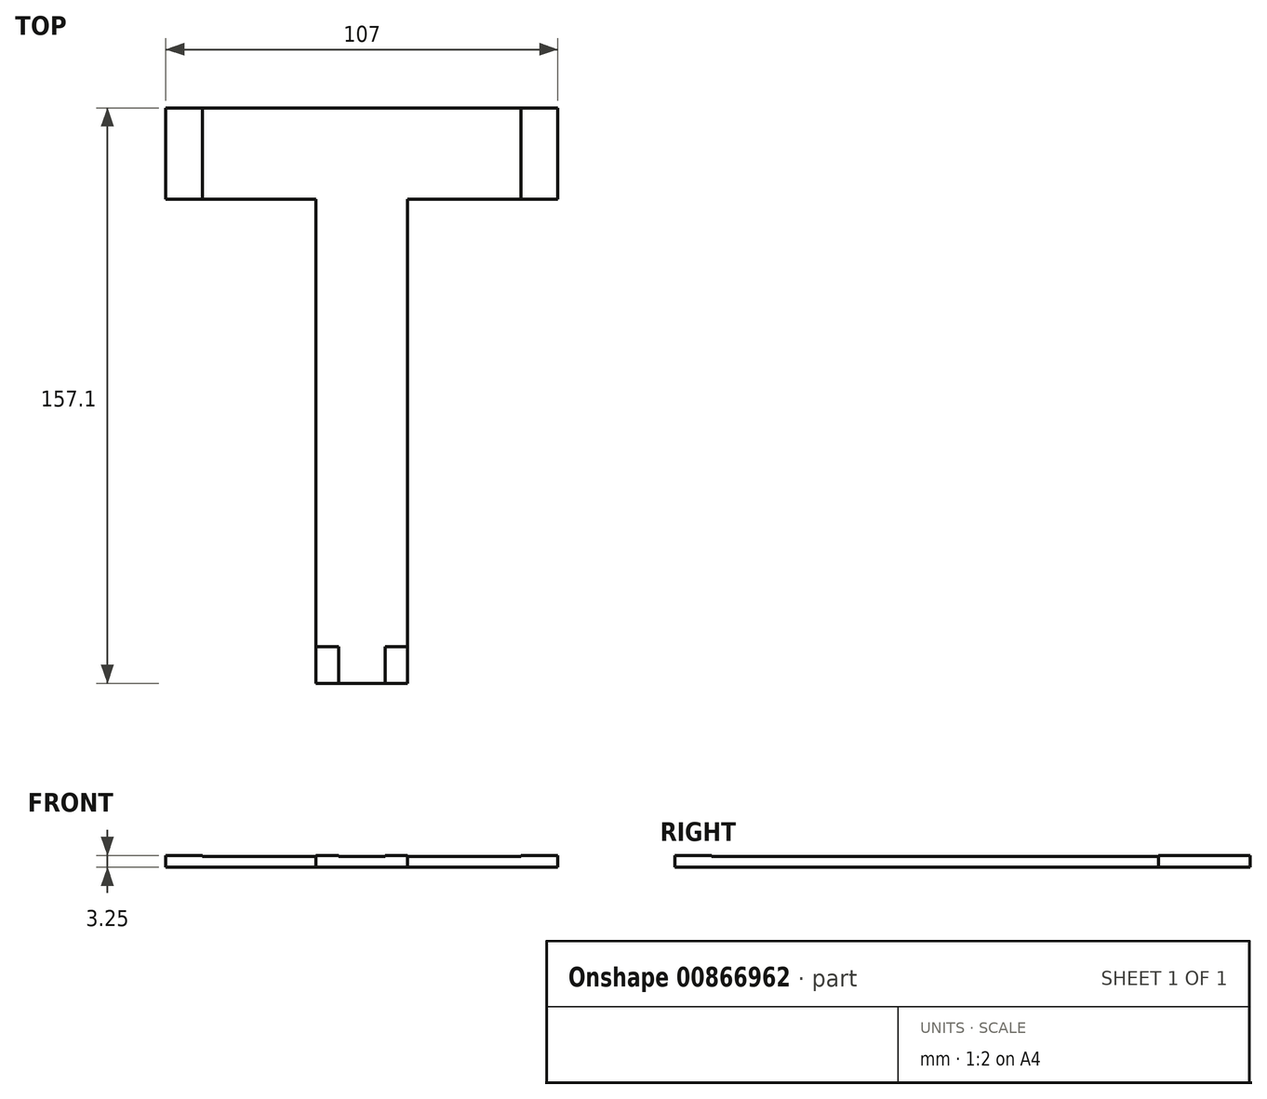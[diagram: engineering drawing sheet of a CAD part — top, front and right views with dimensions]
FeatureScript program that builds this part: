
annotation { "Feature Type Name" : "Feature", "Feature Type Description" : "" }
export const myFeature = defineFeature(function(context is Context, id is Id, definition is map)
    precondition{}
    {
        {
            var Q0;
            Q0=qCreatedBy(makeId("Top.planeOp"),FACE);
            var sketch = newSketch(context, id + "F0", { "sketchPlane" : qUnion([Q0])});
            skLineSegment(sketch, "E0.bottom", {"start": v(13.1, -94.8) * mm, "end": v(-11.9, -94.8) * mm});
            skLineSegment(sketch, "E0.top", {"start": v(13.1, 27.3) * mm, "end": v(-11.9, 27.3) * mm});
            skLineSegment(sketch, "E0.left", {"start": v(13.1, -94.8) * mm, "end": v(13.1, 27.3) * mm});
            skLineSegment(sketch, "E0.right", {"start": v(-11.9, -94.8) * mm, "end": v(-11.9, 27.3) * mm});
            skPoint(sketch, "E0.middle", {"position": v(0.6, -33.75) * mm});
            skLineSegment(sketch, "E1", {"start": v(0.6, 27.3) * mm, "end": v(0.6, 52.3) * mm});
            skLineSegment(sketch, "E2", {"start": v(0.6, 52.3) * mm, "end": v(-42.9, 52.3) * mm});
            skLineSegment(sketch, "E3", {"start": v(-42.9, 52.3) * mm, "end": v(-42.9, 27.3) * mm});
            skLineSegment(sketch, "E4", {"start": v(-42.9, 27.3) * mm, "end": v(-11.9, 27.3) * mm});
            skLineSegment(sketch, "E5", {"start": v(0.6, 52.3) * mm, "end": v(44.1, 52.3) * mm});
            skLineSegment(sketch, "E6", {"start": v(44.1, 52.3) * mm, "end": v(44.1, 27.3) * mm});
            skLineSegment(sketch, "E7", {"start": v(44.1, 27.3) * mm, "end": v(13.1, 27.3) * mm});
            skLineSegment(sketch, "E8", {"start": v(44.1, 52.3) * mm, "end": v(54.1, 52.3) * mm});
            skLineSegment(sketch, "E9", {"start": v(54.1, 52.3) * mm, "end": v(54.1, 27.3) * mm});
            skLineSegment(sketch, "E10", {"start": v(54.1, 27.3) * mm, "end": v(44.1, 27.3) * mm});
            skLineSegment(sketch, "E11", {"start": v(39.1, 52.3) * mm, "end": v(39.1, 27.3) * mm});
            skLineSegment(sketch, "E12", {"start": v(-36.9, 52.3) * mm, "end": v(-36.9, 27.3) * mm});
            skLineSegment(sketch, "E13", {"start": v(-42.9, 52.3) * mm, "end": v(-52.9, 52.3) * mm});
            skLineSegment(sketch, "E14", {"start": v(-52.9, 52.3) * mm, "end": v(-52.9, 27.3) * mm});
            skLineSegment(sketch, "E15", {"start": v(-52.9, 27.3) * mm, "end": v(-42.9, 27.3) * mm});
            skLineSegment(sketch, "E16", {"start": v(-18.95, -94.8) * mm, "end": v(-18.95, -89.8) * mm});
            skLineSegment(sketch, "E17", {"start": v(-11.9, -94.8) * mm, "end": v(-11.9, -104.8) * mm});
            skLineSegment(sketch, "E18", {"start": v(-11.9, -104.8) * mm, "end": v(13.1, -104.8) * mm});
            skLineSegment(sketch, "E19", {"start": v(13.1, -104.8) * mm, "end": v(13.1, -94.8) * mm});
            skLineSegment(sketch, "E20", {"start": v(-11.9, -89.8) * mm, "end": v(13.1, -89.8) * mm});
            skLineSegment(sketch, "E21", {"start": v(-5.76, -89.8) * mm, "end": v(-5.76, -104.8) * mm});
            skLineSegment(sketch, "E22", {"start": v(6.94, -89.8) * mm, "end": v(6.94, -104.8) * mm});
            skSolve(sketch);
        }
        {
            var Q0;
            {var subQ0=sQuery(id+"F0.wireOp",EDGE,"E3");Q0=makeQuery(id+"F0.imprint","IMPRINT",FACE,{"disambiguationData":[TD([[makeQuery(id+"F0.imprint","IMPRINT",EDGE,{"derivedFrom":subQ0}),1.0]])]});}
            var Q1;
            {var subQ1=sQuery(id+"F0.wireOp",EDGE,"E1");Q1=makeQuery(id+"F0.imprint","IMPRINT",FACE,{"disambiguationData":[TD([[makeQuery(id+"F0.imprint","IMPRINT",EDGE,{"derivedFrom":subQ1}),1.0]])]});}
            var Q2;
            {var subQ1=sQuery(id+"F0.wireOp",EDGE,"E1");Q2=makeQuery(id+"F0.imprint","IMPRINT",FACE,{"disambiguationData":[TD([[makeQuery(id+"F0.imprint","IMPRINT",EDGE,{"derivedFrom":subQ1}),-1.0]])]});}
            var Q3;
            {var subQ0=sQuery(id+"F0.wireOp",EDGE,"E6");Q3=makeQuery(id+"F0.imprint","IMPRINT",FACE,{"disambiguationData":[TD([[makeQuery(id+"F0.imprint","IMPRINT",EDGE,{"derivedFrom":subQ0}),-1.0]])]});}
            var Q4;
            {var subQ0=sQuery(id+"F0.wireOp",EDGE,"E22");var subQ1=sQuery(id+"F0.wireOp",EDGE,"E0.bottom");var subQ2=makeQuery(id+"F0.imprint","INTERSECT",VERTEX,{"derivedFrom":[subQ1,subQ0]});Q4=makeQuery(id+"F0.imprint","IMPRINT",FACE,{"disambiguationData":[TD([[makeQuery(id+"F0.imprint","IMPRINT",EDGE,{"disambiguationData":[TD([[subQ2,-1.0]])],"derivedFrom":subQ1}),1.0]])]});}
            var Q5;
            {var subQ0=sQuery(id+"F0.wireOp",EDGE,"E22");var subQ1=sQuery(id+"F0.wireOp",EDGE,"E0.bottom");var subQ2=makeQuery(id+"F0.imprint","INTERSECT",VERTEX,{"derivedFrom":[subQ1,subQ0]});Q5=makeQuery(id+"F0.imprint","IMPRINT",FACE,{"disambiguationData":[TD([[makeQuery(id+"F0.imprint","IMPRINT",EDGE,{"disambiguationData":[TD([[subQ2,-1.0]])],"derivedFrom":subQ1}),-1.0]])]});}
            var Q6;
            {var subQ0=sQuery(id+"F0.wireOp",EDGE,"E0.left");var subQ5=sQuery(id+"F0.wireOp",EDGE,"E20");var subQ6=makeQuery(id+"F0.imprint","INTERSECT",VERTEX,{"derivedFrom":[subQ0,subQ5]});Q6=makeQuery(id+"F0.imprint","IMPRINT",FACE,{"disambiguationData":[TD([[makeQuery(id+"F0.imprint","IMPRINT",EDGE,{"disambiguationData":[TD([[subQ6,1.0]])],"derivedFrom":subQ5}),-1.0]])]});}
            var Q7;
            {var subQ3=sQuery(id+"F0.wireOp",EDGE,"E20");var subQ5=sQuery(id+"F0.wireOp",EDGE,"E0.right");var subQ8=makeQuery(id+"F0.imprint","INTERSECT",VERTEX,{"derivedFrom":[subQ5,subQ3]});Q7=makeQuery(id+"F0.imprint","IMPRINT",FACE,{"disambiguationData":[TD([[makeQuery(id+"F0.imprint","IMPRINT",EDGE,{"disambiguationData":[TD([[subQ8,-1.0]])],"derivedFrom":subQ3}),1.0]])]});}
            var Q8;
            {var subQ0=sQuery(id+"F0.wireOp",EDGE,"E0.right");var subQ5=sQuery(id+"F0.wireOp",EDGE,"E20");var subQ6=makeQuery(id+"F0.imprint","INTERSECT",VERTEX,{"derivedFrom":[subQ0,subQ5]});Q8=makeQuery(id+"F0.imprint","IMPRINT",FACE,{"disambiguationData":[TD([[makeQuery(id+"F0.imprint","IMPRINT",EDGE,{"disambiguationData":[TD([[subQ6,-1.0]])],"derivedFrom":subQ5}),-1.0]])]});}
            extrude(context, id + "F1", {"entities" : qUnion([Q0, Q1, Q2, Q3, Q4, Q5, Q6, Q7, Q8]), "depth" : 3 * mm, "offsetDistance" : 25 * mm});
        }
        {
            var Q0;
            {var subQ0=sQuery(id+"F0.wireOp",EDGE,"E19");Q0=makeQuery(id+"F0.imprint","IMPRINT",FACE,{"disambiguationData":[TD([[makeQuery(id+"F0.imprint","IMPRINT",EDGE,{"derivedFrom":subQ0}),1.0]])]});}
            var Q1;
            {var subQ0=sQuery(id+"F0.wireOp",EDGE,"E17");Q1=makeQuery(id+"F0.imprint","IMPRINT",FACE,{"disambiguationData":[TD([[makeQuery(id+"F0.imprint","IMPRINT",EDGE,{"derivedFrom":subQ0}),1.0]])]});}
            var Q2;
            Q2=makeQuery(id+"F0.imprint","IMPRINT",FACE,{"disambiguationData":[TD([[makeQuery(id+"F0.imprint","IMPRINT",EDGE,{"derivedFrom":sQuery(id+"F0.wireOp",EDGE,"E3")}),-1.0]])]});
            var Q3;
            Q3=makeQuery(id+"F0.imprint","IMPRINT",FACE,{"disambiguationData":[TD([[makeQuery(id+"F0.imprint","IMPRINT",EDGE,{"derivedFrom":sQuery(id+"F0.wireOp",EDGE,"E6")}),1.0]])]});
            extrude(context, id + "F2", {"entities" : qUnion([Q0, Q1, Q2, Q3]), "operationType" : NewBodyOperationType.ADD, "depth" : 3.25 * mm, "offsetDistance" : 25 * mm});
        }
    });
